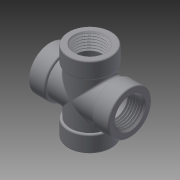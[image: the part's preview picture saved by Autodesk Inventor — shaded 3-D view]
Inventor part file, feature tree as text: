
AUTODESK INVENTOR PART (.ipt)
format: ipt  version: 2014 (Build 180170000, 170)  size: 3,510,784 bytes
history: native  units: in
note: dims shown in document units (in); Inventor stores cm internally (conversion verified against a paired STEP export)
features: other x2, sketch x1, imported_body x1
ambient origin geometry x8: Origin, YZ Plane, XZ Plane, XY Plane, X Axis, Y Axis, Z Axis, Center Point
bodies: Body1 (feature_tree)
feature tree (4):
  parser-record x1  (decoder bookkeeping rows leaked as tree rows — omitted from the tree; the rows remain in map.json)
  other  "4464K314_TYPE 304 STAINLESS STL THREADED PIPE FITTING1"
  sketch  "Sketch1"
  imported_body  "Base1"
